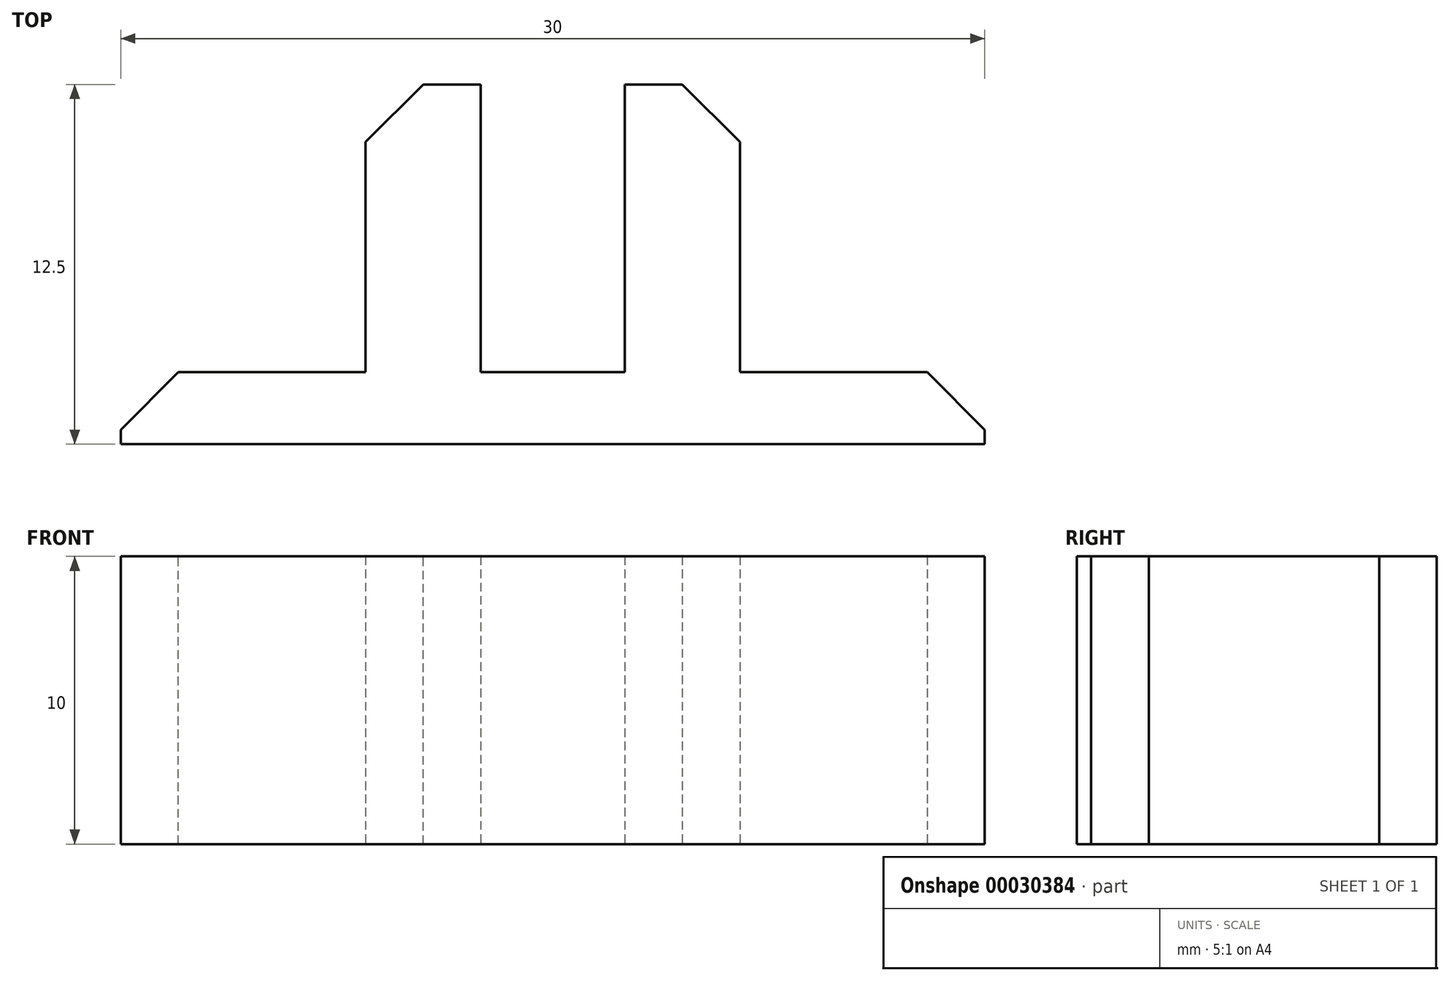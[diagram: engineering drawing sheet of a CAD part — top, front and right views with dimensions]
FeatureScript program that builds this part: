
annotation { "Feature Type Name" : "Feature", "Feature Type Description" : "" }
export const myFeature = defineFeature(function(context is Context, id is Id, definition is map)
    precondition{}
    {
        {
            var Q0;
            Q0=qCreatedBy(makeId("Top.planeOp"),FACE);
            var sketch = newSketch(context, id + "F0", { "sketchPlane" : qUnion([Q0])});
            skLineSegment(sketch, "E0", {"start": v(0, 0) * mm, "end": v(15, 0) * mm});
            skLineSegment(sketch, "E1", {"start": v(15, 0) * mm, "end": v(15, 2.5) * mm});
            skLineSegment(sketch, "E2", {"start": v(15, 2.5) * mm, "end": v(6.5, 2.5) * mm});
            skLineSegment(sketch, "E3", {"start": v(6.5, 2.5) * mm, "end": v(6.5, 12.5) * mm});
            skLineSegment(sketch, "E4", {"start": v(6.5, 12.5) * mm, "end": v(2.5, 12.5) * mm});
            skLineSegment(sketch, "E5", {"start": v(2.5, 12.5) * mm, "end": v(2.5, 2.5) * mm});
            skLineSegment(sketch, "E6", {"start": v(2.5, 2.5) * mm, "end": v(0, 2.5) * mm});
            skLineSegment(sketch, "E7.MirrorCS", {"start": v(-6.5, 12.5) * mm, "end": v(-2.5, 12.5) * mm});
            skLineSegment(sketch, "E8.MirrorCS", {"start": v(-2.5, 12.5) * mm, "end": v(-2.5, 2.5) * mm});
            skLineSegment(sketch, "E9.MirrorCS", {"start": v(-2.5, 2.5) * mm, "end": v(0, 2.5) * mm});
            skLineSegment(sketch, "E10.MirrorCS", {"start": v(0, 0) * mm, "end": v(-15, 0) * mm});
            skLineSegment(sketch, "E11.MirrorCS", {"start": v(-15, 0) * mm, "end": v(-15, 2.5) * mm});
            skLineSegment(sketch, "E12.MirrorCS", {"start": v(-15, 2.5) * mm, "end": v(-6.5, 2.5) * mm});
            skLineSegment(sketch, "E13.MirrorCS", {"start": v(-6.5, 2.5) * mm, "end": v(-6.5, 12.5) * mm});
            skSolve(sketch);
        }
        {
            var Q0;
            Q0 = qSketchRegion(id + "F0", true);
            extrude(context, id + "F1", {"entities" : qUnion([Q0]), "depth" : 10 * mm});
        }
        {
            var Q0;
            Q0=makeQuery(id+"F1.opExtrude","SWEPT_EDGE",EDGE,{"disambiguationData":[OSD([sQuery(id+"F0.wireOp",EDGE,"E7.MirrorCS"),sQuery(id+"F0.wireOp",EDGE,"E13.MirrorCS")])]});
            var Q1;
            Q1=makeQuery(id+"F1.opExtrude","SWEPT_EDGE",EDGE,{"disambiguationData":[OSD([sQuery(id+"F0.wireOp",EDGE,"E11.MirrorCS"),sQuery(id+"F0.wireOp",EDGE,"E12.MirrorCS")])]});
            var Q2;
            Q2=makeQuery(id+"F1.opExtrude","SWEPT_EDGE",EDGE,{"disambiguationData":[OSD([sQuery(id+"F0.wireOp",EDGE,"E3"),sQuery(id+"F0.wireOp",EDGE,"E4")])]});
            var Q3;
            Q3=makeQuery(id+"F1.opExtrude","SWEPT_EDGE",EDGE,{"disambiguationData":[OSD([sQuery(id+"F0.wireOp",EDGE,"E1"),sQuery(id+"F0.wireOp",EDGE,"E2")])]});
            chamfer(context, id + "F2", {"entities" : qUnion([Q0, Q1, Q2, Q3]), "width" : 2 * mm, "tangentPropagation" : true});
        }
    });
